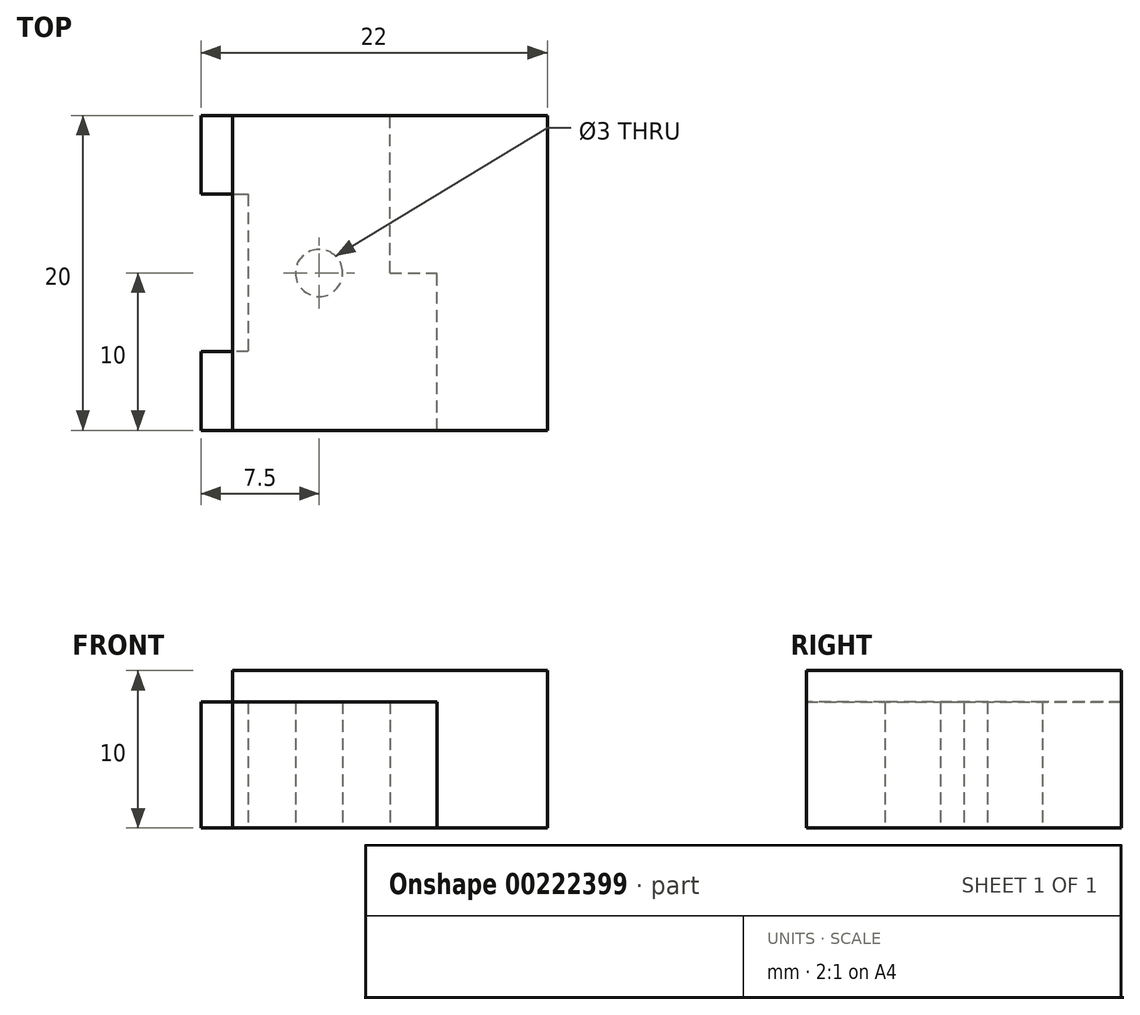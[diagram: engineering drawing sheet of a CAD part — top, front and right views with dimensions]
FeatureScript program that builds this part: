
annotation { "Feature Type Name" : "Feature", "Feature Type Description" : "" }
export const myFeature = defineFeature(function(context is Context, id is Id, definition is map)
    precondition{}
    {
        {
            var Q0;
            Q0=qCreatedBy(makeId("Top.planeOp"),FACE);
            var sketch = newSketch(context, id + "F0", { "sketchPlane" : qUnion([Q0])});
            skLineSegment(sketch, "E0.bottom", {"start": v(10, -10) * mm, "end": v(-10, -10) * mm});
            skLineSegment(sketch, "E0.top", {"start": v(10, 10) * mm, "end": v(-10, 10) * mm});
            skLineSegment(sketch, "E0.left", {"start": v(10, -10) * mm, "end": v(10, 10) * mm});
            skLineSegment(sketch, "E0.right", {"start": v(-10, -10) * mm, "end": v(-10, 10) * mm});
            skPoint(sketch, "E0.middle", {"position": v(0, 0) * mm});
            skSolve(sketch);
        }
        {
            var Q0;
            Q0 = qSketchRegion(id + "F0", true);
            extrude(context, id + "F1", {"entities" : qUnion([Q0]), "depth" : 10 * mm});
        }
        {
            var Q0;
            Q0=qCreatedBy(makeId("Top.planeOp"),FACE);
            var sketch = newSketch(context, id + "F2", { "sketchPlane" : qUnion([Q0])});
            skLineSegment(sketch, "E1.bottom", {"start": v(3, -10) * mm, "end": v(-12, -10) * mm});
            skLineSegment(sketch, "E1.top", {"start": v(0, 10) * mm, "end": v(-12, 10) * mm});
            skLineSegment(sketch, "E1.left", {"start": v(3, -10) * mm, "end": v(3, 0) * mm});
            skLineSegment(sketch, "E1.right", {"start": v(-12, -10) * mm, "end": v(-12, 10) * mm, "construction": true});
            skPoint(sketch, "E1.middle", {"position": v(0, 0) * mm});
            skLineSegment(sketch, "E2.bottom", {"start": v(0, 0) * mm, "end": v(3, 0) * mm});
            skLineSegment(sketch, "E2.left", {"start": v(0, 0) * mm, "end": v(0, 10) * mm});
            skLineSegment(sketch, "E3", {"start": v(0, 0) * mm, "end": v(-12, 0) * mm, "construction": true});
            skLineSegment(sketch, "E4", {"start": v(-12, 10) * mm, "end": v(-12, 5) * mm});
            skLineSegment(sketch, "E5", {"start": v(-12, 5) * mm, "end": v(-9, 5) * mm});
            skLineSegment(sketch, "E6", {"start": v(-9, 5) * mm, "end": v(-9, -5) * mm});
            skLineSegment(sketch, "E7", {"start": v(-9, -5) * mm, "end": v(-12, -5) * mm});
            skLineSegment(sketch, "E8", {"start": v(-12, -5) * mm, "end": v(-12, -10) * mm});
            skCircle(sketch, "E9", {"center": v(-4.5, 0) * mm, "radius": 1.5 * mm});
            skSolve(sketch);
        }
        {
            var Q0;
            Q0 = qSketchRegion(id + "F2", true);
            extrude(context, id + "F3", {"entities" : qUnion([Q0]), "depth" : 8 * mm});
        }
    });
